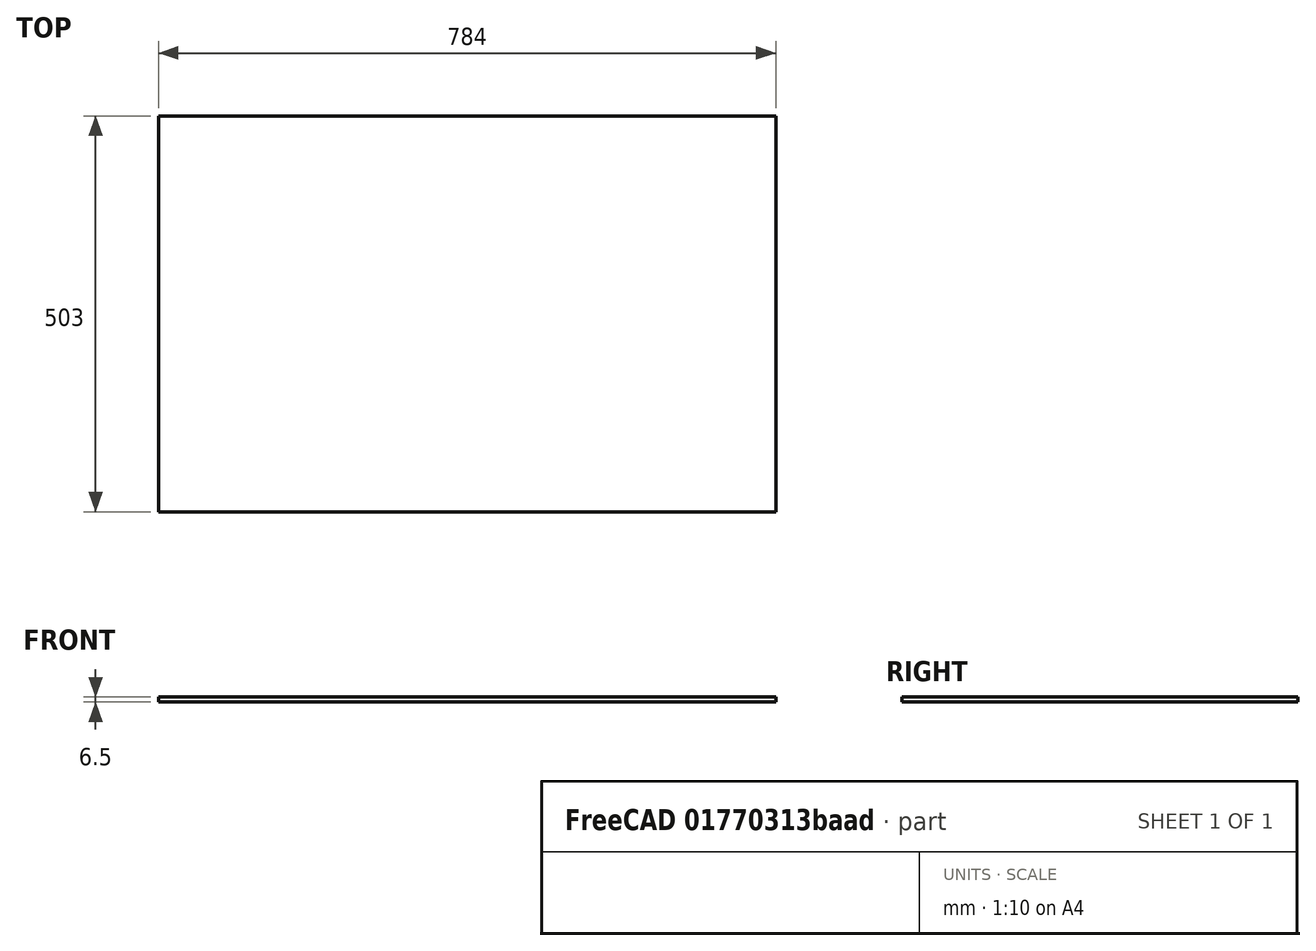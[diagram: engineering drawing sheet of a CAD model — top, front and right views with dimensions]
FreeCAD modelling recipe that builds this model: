
FCSTD DOCUMENT  (FreeCAD 1.0R39109 (Git))
Label: 74_drawer_box_back
License: All rights reserved
LicenseURL: http://en.wikipedia.org/wiki/All_rights_reserved
objects: Spreadsheet::Sheet×1, Sketcher::SketchObject×1, PartDesign::Pad×1, PartDesign::Body×1
note: 6 computed .brp shape members not serialized (recipe doc carries the construction recipe); baked Part::Feature solids carry a one-line shape summary decoded from their .brp

FEATURE [Spreadsheet::Sheet] Spreadsheet
  cells = A2='length; B2(length)=784; A3='width; B3(width)=503; A4='height; B4(height)=6.5
FEATURE [Sketcher::SketchObject] Sketch
  ArcFitTolerance = 0
  AttachmentSupport = -> [XY_Plane]
  FullyConstrained = true
  MakeInternals = false
  MapMode = 5
  expr: Constraints[11] = Spreadsheet.length
  expr: Constraints[12] = Spreadsheet.width
  sketch-geometry (5):
    g0: LineSegment StartX=-392 StartY=251.5 StartZ=0 EndX=392 EndY=251.5 EndZ=0
    g1: LineSegment StartX=392 StartY=251.5 StartZ=0 EndX=392 EndY=-251.5 EndZ=0
    g2: LineSegment StartX=392 StartY=-251.5 StartZ=0 EndX=-392 EndY=-251.5 EndZ=0
    g3: LineSegment StartX=-392 StartY=-251.5 StartZ=0 EndX=-392 EndY=251.5 EndZ=0
    g4: LineSegment [constr] StartX=-392 StartY=251.5 StartZ=0 EndX=392 EndY=-251.5 EndZ=0
  constraints (13):
    c: Coincident(g0,g1)
    c: Coincident(g1,g2)
    c: Coincident(g2,g3)
    c: Coincident(g3,g0)
    c: Horizontal(g0)
    c: Horizontal(g2)
    c: Vertical(g1)
    c: Vertical(g3)
    c: Coincident(g4,g1)
    c: Coincident(g0,g4)
    c: Symmetric(g0,g1,g-1)
    c: Distance(g0,g0) = 784
    c: Distance(g0,g2) = 503
FEATURE [PartDesign::Pad] Pad
  Direction = (0,0,1)
  Length = 6.5
  Length2 = 10
  Profile = -> Sketch
  ReferenceAxis = -> Sketch [N_Axis]
  Suppressed = false
  Type = 0
  expr: Length = Spreadsheet.height
FEATURE [PartDesign::Body] Body
  AllowCompound = false
  Group = -> [Sketch,Pad]
  Origin = -> Origin
  Tip = -> Pad
